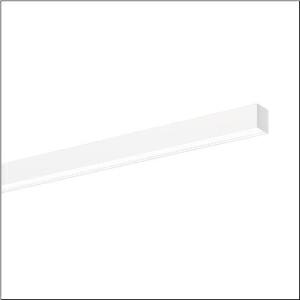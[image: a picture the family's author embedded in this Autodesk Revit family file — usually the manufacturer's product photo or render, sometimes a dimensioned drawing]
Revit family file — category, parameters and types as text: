
# Revit family: silica_21_51mx20dc35wb
name_source: partatom
category: Lighting Fixtures
units: mm (PartAtom-declared; Revit-internal decimal feet)

## family parameters
Cut with Voids When Loaded = No
Host = Face
Light Source = No
Part Type = Normal
Room Calculation Point = No
Round Connector Dimension = Use Diameter
Shared = No

## types (1)
- --- (1 x LED, 6000 lm, 42.6 W, 3000K)
    Apparent Load = 43 VA
    CIE Flux Codes = 48 79 96 100 100
    Color Rendering = 80
    Color Temperature = 3000K
    Default Elevation = 1800 mm
    Description = Silica 21, office luminaire, primary optical cover: cover, of PMMA, opal, light emission: direct distribution, primary light characteristic: symmetric, installation type: surface-mounted, LED, rated luminous flux: 6.000lm, luminous efficacy: 141lm/W, light colour: 830, colour temperature: 3000K, control gear: DALI 2, with terminal, 3+2-pole, max. 2.5mm², mains connection: 220..240V, AC, 50/60Hz, rated input power: 42.6W, luminaire housing, of aluminium, traffic white (RAL 9016), length: 3.004mm, width: 53mm, height: 53mm, protection rating (complete): IP20, insulation class (complete): insulation class I (protective earthing), certification: CE, permissible operating ambient temperature: 0..+35°C, standard: EN 50419, packaging unit: 1 piece
    Height = 53 mm
    Lamp = 1 x LED
    Lamp Light Flux = 6000 lm
    Lamp Power = 42.6 W
    Lamp count = 1
    Length = 3004 mm
    Luminous efficacy = 141 lm/W
    Manufacturer = Siteco
    ModVariant = No
    Model = 51MX20DC35WB
    Mounting Place = Ceiling
    Mounting Type = Surface mounted
    Number of Poles = 1
    OnlyDefault = Yes
    Power Factor = 1
    Product Name = Silica 21
    Product group = office luminaire | ceiling mounted
    ProductGroupID = 301
    Protection Class = Protection class I
    Protection Degree = IP 20
    RLX_Detail_Level = 1
    RLX_Emergency_Light_Flux = 0 lm
    RLX_Emergency_Type = 0
    RLX_Emergency_Type_DB = No
    RlxData = <blob elided: 23953 chars, md5=421aa550>
    Socket = socket
    Standby Power = 0 W
    System Light Flux = 6000 lm
    System Power = 43 W
    Type Comments = factory setting: luminous flux: 100 % | dim-lin: 254 | 233 mA
    Type Image = l_1335877.jpg
    URL = http://relux.com
    VarID = @adj_119651
    Voltage = 0 V
    Weight = 0.00 kg
    Width = 53 mm

## geometry (parser evidence)
native form markers: Blend x4, Sweep x10
no freeform markers — native parametric forms only
